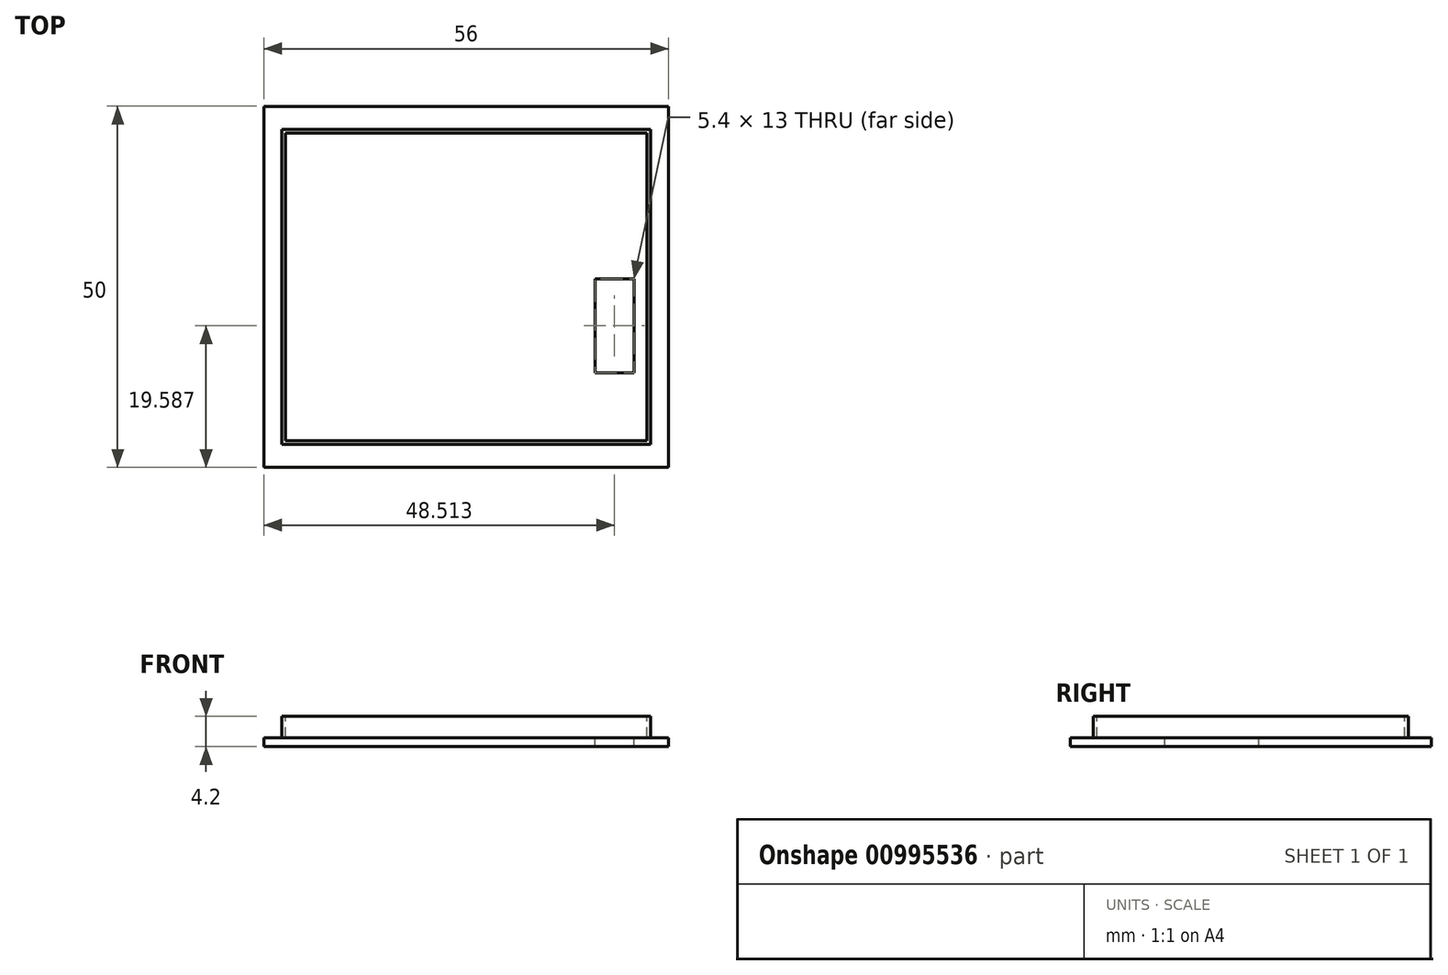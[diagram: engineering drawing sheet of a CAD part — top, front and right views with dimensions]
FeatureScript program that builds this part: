
annotation { "Feature Type Name" : "Feature", "Feature Type Description" : "" }
export const myFeature = defineFeature(function(context is Context, id is Id, definition is map)
    precondition{}
    {
        {
            var Q0;
            Q0=qCreatedBy(makeId("Top.planeOp"),FACE);
            var sketch = newSketch(context, id + "F0", { "sketchPlane" : qUnion([Q0])});
            skLineSegment(sketch, "E0.bottom", {"start": v(-68.98, 18.88) * mm, "end": v(-12.98, 18.88) * mm});
            skLineSegment(sketch, "E0.top", {"start": v(-68.98, -31.12) * mm, "end": v(-12.98, -31.12) * mm});
            skLineSegment(sketch, "E0.left", {"start": v(-68.98, 18.88) * mm, "end": v(-68.98, -31.12) * mm});
            skLineSegment(sketch, "E0.right", {"start": v(-12.98, 18.88) * mm, "end": v(-12.98, -31.12) * mm});
            skSolve(sketch);
        }
        {
            var Q0;
            Q0=makeQuery(id+"F0.imprint","IMPRINT",FACE,{"disambiguationData":[TD([[makeQuery(id+"F0.imprint","IMPRINT",EDGE,{"derivedFrom":sQuery(id+"F0.wireOp",EDGE,"E0.bottom")}),-1.0]])]});
            extrude(context, id + "F1", {"entities" : qUnion([Q0]), "depth" : 1.2 * mm, "offsetDistance" : 25 * mm});
        }
        {
            var Q0;
            Q0=makeQuery(id+"F1.opExtrude","CAP_FACE",FACE,{"disambiguationData":[OSD([sQuery(id+"F0.wireOp",EDGE,"E0.bottom"),sQuery(id+"F0.wireOp",EDGE,"E0.top"),sQuery(id+"F0.wireOp",EDGE,"E0.left"),sQuery(id+"F0.wireOp",EDGE,"E0.right")])],"isStart":false});
            var sketch = newSketch(context, id + "F2", { "sketchPlane" : qUnion([Q0])});
            skLineSegment(sketch, "E1.bottom", {"start": v(-23.17, -18.03) * mm, "end": v(-17.77, -18.03) * mm});
            skLineSegment(sketch, "E1.top", {"start": v(-23.17, -5.03) * mm, "end": v(-17.77, -5.03) * mm});
            skLineSegment(sketch, "E1.left", {"start": v(-23.17, -18.03) * mm, "end": v(-23.17, -5.03) * mm});
            skLineSegment(sketch, "E1.right", {"start": v(-17.77, -18.03) * mm, "end": v(-17.77, -5.03) * mm});
            skSolve(sketch);
        }
        {
            var Q0;
            Q0=makeQuery(id+"F2.imprint","IMPRINT",FACE,{"disambiguationData":[TD([[makeQuery(id+"F2.imprint","IMPRINT",EDGE,{"derivedFrom":sQuery(id+"F2.wireOp",EDGE,"E1.bottom")}),1.0]])]});
            extrude(context, id + "F3", {"entities" : qUnion([Q0]), "operationType" : NewBodyOperationType.REMOVE, "oppositeDirection" : true, "depth" : 1.2 * mm, "offsetDistance" : 25 * mm});
        }
        {
            var Q0;
            Q0=makeQuery(id+"F1.opExtrude","CAP_FACE",FACE,{"disambiguationData":[OSD([sQuery(id+"F0.wireOp",EDGE,"E0.bottom"),sQuery(id+"F0.wireOp",EDGE,"E0.top"),sQuery(id+"F0.wireOp",EDGE,"E0.left"),sQuery(id+"F0.wireOp",EDGE,"E0.right")])],"isStart":false});
            var sketch = newSketch(context, id + "F4", { "sketchPlane" : qUnion([Q0])});
            skLineSegment(sketch, "E2.bottom", {"start": v(-66.48, 15.68) * mm, "end": v(-15.48, 15.68) * mm});
            skLineSegment(sketch, "E2.top", {"start": v(-66.48, -27.92) * mm, "end": v(-15.48, -27.92) * mm});
            skLineSegment(sketch, "E2.left", {"start": v(-66.48, 15.68) * mm, "end": v(-66.48, -27.92) * mm});
            skLineSegment(sketch, "E2.right", {"start": v(-15.48, 15.68) * mm, "end": v(-15.48, -27.92) * mm});
            skPoint(sketch, "E2.middle", {"position": v(-40.98, -6.12) * mm});
            skPoint(sketch, "E2.middle.positionSnap0", {"position": v(-68.98, -6.12) * mm});
            skPoint(sketch, "E2.middle.positionSnap1", {"position": v(-40.98, 18.88) * mm});
            skPoint(sketch, "E2.centerSnap0", {"position": v(-68.98, -6.12) * mm});
            skPoint(sketch, "E2.centerSnap1", {"position": v(-40.98, 18.88) * mm});
            skSolve(sketch);
        }
        {
            var Q0;
            Q0=makeQuery(id+"F4.imprint","IMPRINT",FACE,{"disambiguationData":[TD([[makeQuery(id+"F4.imprint","IMPRINT",EDGE,{"derivedFrom":sQuery(id+"F4.wireOp",EDGE,"E2.bottom")}),-1.0]])]});
            extrude(context, id + "F5", {"entities" : qUnion([Q0]), "operationType" : NewBodyOperationType.ADD, "depth" : 3 * mm, "offsetDistance" : 25 * mm});
        }
        {
            var Q0;
            Q0=makeQuery(id+"F5.opExtrude","CAP_FACE",FACE,{"disambiguationData":[OSD([sQuery(id+"F2.wireOp",EDGE,"E1.bottom"),sQuery(id+"F2.wireOp",EDGE,"E1.top"),sQuery(id+"F2.wireOp",EDGE,"E1.left"),sQuery(id+"F2.wireOp",EDGE,"E1.right"),sQuery(id+"F4.wireOp",EDGE,"E2.bottom"),sQuery(id+"F4.wireOp",EDGE,"E2.top"),sQuery(id+"F4.wireOp",EDGE,"E2.left"),sQuery(id+"F4.wireOp",EDGE,"E2.right")])],"isStart":false});
            var sketch = newSketch(context, id + "F6", { "sketchPlane" : qUnion([Q0])});
            skLineSegment(sketch, "E3.bottom", {"start": v(-65.98, 15.18) * mm, "end": v(-15.98, 15.18) * mm});
            skLineSegment(sketch, "E3.top", {"start": v(-65.98, -27.42) * mm, "end": v(-15.98, -27.42) * mm});
            skLineSegment(sketch, "E3.left", {"start": v(-65.98, 15.18) * mm, "end": v(-65.98, -27.42) * mm});
            skLineSegment(sketch, "E3.right", {"start": v(-15.98, 15.18) * mm, "end": v(-15.98, -27.42) * mm});
            skPoint(sketch, "E3.middle", {"position": v(-40.98, -6.12) * mm});
            skPoint(sketch, "E3.middle.positionSnap0", {"position": v(-40.98, 15.68) * mm});
            skPoint(sketch, "E3.middle.positionSnap1", {"position": v(-66.48, -6.12) * mm});
            skPoint(sketch, "E3.centerSnap0", {"position": v(-40.98, 15.68) * mm});
            skPoint(sketch, "E3.centerSnap1", {"position": v(-66.48, -6.12) * mm});
            skSolve(sketch);
        }
        {
            var Q0;
            Q0=makeQuery(id+"F6.imprint","IMPRINT",FACE,{"disambiguationData":[TD([[makeQuery(id+"F6.imprint","IMPRINT",EDGE,{"derivedFrom":sQuery(id+"F6.wireOp",EDGE,"E3.bottom")}),-1.0]])]});
            extrude(context, id + "F7", {"entities" : qUnion([Q0]), "operationType" : NewBodyOperationType.REMOVE, "oppositeDirection" : true, "depth" : 3 * mm, "offsetDistance" : 25 * mm});
        }
    });
